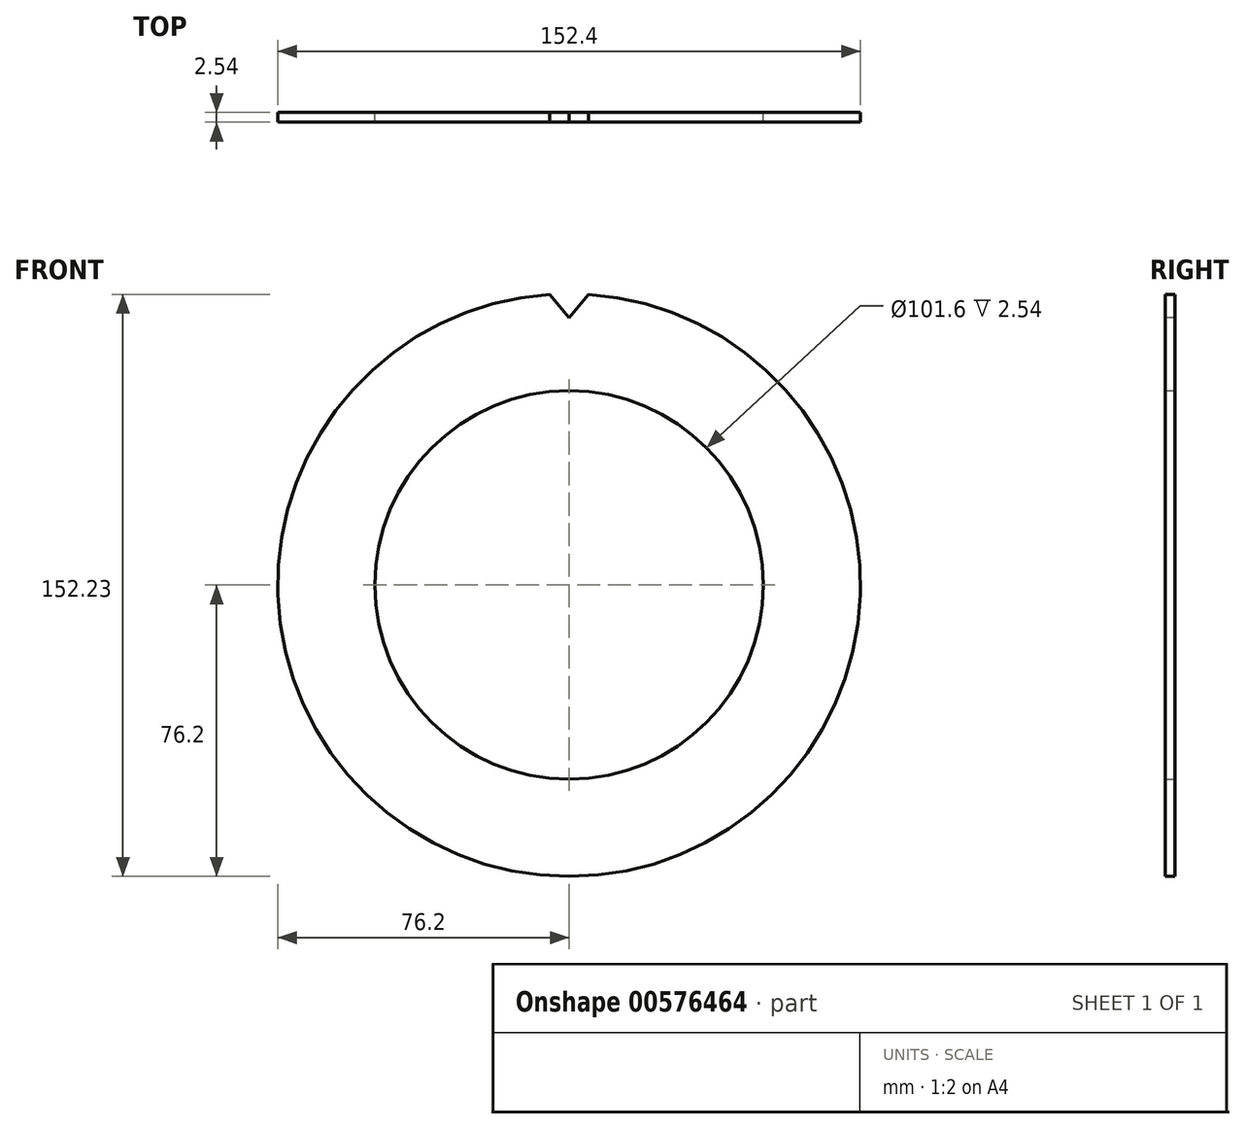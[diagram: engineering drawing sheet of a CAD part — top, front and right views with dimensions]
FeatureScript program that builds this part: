
annotation { "Feature Type Name" : "Feature", "Feature Type Description" : "" }
export const myFeature = defineFeature(function(context is Context, id is Id, definition is map)
    precondition{}
    {
        {
            var Q0;
            Q0=qCreatedBy(makeId("Front.planeOp"),FACE);
            var sketch = newSketch(context, id + "F0", { "sketchPlane" : qUnion([Q0])});
            skCircle(sketch, "E0", {"center": v(0, 0) * mm, "radius": 76.2 * mm});
            skCircle(sketch, "E1", {"center": v(0, 0) * mm, "radius": 50.8 * mm});
            skSolve(sketch);
        }
        {
            var Q0;
            Q0 = qSketchRegion(id + "F0", true);
            extrude(context, id + "F1", {"entities" : qUnion([Q0]), "depth" : 2.54 * mm, "offsetDistance" : 25.4 * mm});
        }
        {
            var Q0;
            Q0=makeQuery(id+"F1.opExtrude","CAP_FACE",FACE,{"disambiguationData":[OSD([sQuery(id+"F0.wireOp",EDGE,"E0"),sQuery(id+"F0.wireOp",EDGE,"E1")])],"isStart":false});
            var sketch = newSketch(context, id + "F2", { "sketchPlane" : qUnion([Q0])});
            skCircle(sketch, "E2", {"center": v(0, 0) * mm, "radius": 69.85 * mm, "construction": true});
            skLineSegment(sketch, "E3", {"start": v(0, 69.85) * mm, "end": v(-6.22, 77.47) * mm});
            skLineSegment(sketch, "E4", {"start": v(-6.22, 77.47) * mm, "end": v(6.22, 77.47) * mm});
            skLineSegment(sketch, "E5", {"start": v(6.22, 77.47) * mm, "end": v(0, 69.85) * mm});
            skLineSegment(sketch, "E6.anchor1", {"start": v(0, 0) * mm, "end": v(0, 69.85) * mm, "construction": true});
            skLineSegment(sketch, "E6.anchor2", {"start": v(0, 0) * mm, "end": v(0, 69.85) * mm, "construction": true});
            skSolve(sketch);
        }
        {
            var Q0;
            Q0 = qSketchRegion(id + "F2", true);
            extrude(context, id + "F3", {"entities" : qUnion([Q0]), "operationType" : NewBodyOperationType.REMOVE, "oppositeDirection" : true, "depth" : 25.4 * mm, "offsetDistance" : 25.4 * mm});
        }
    });
